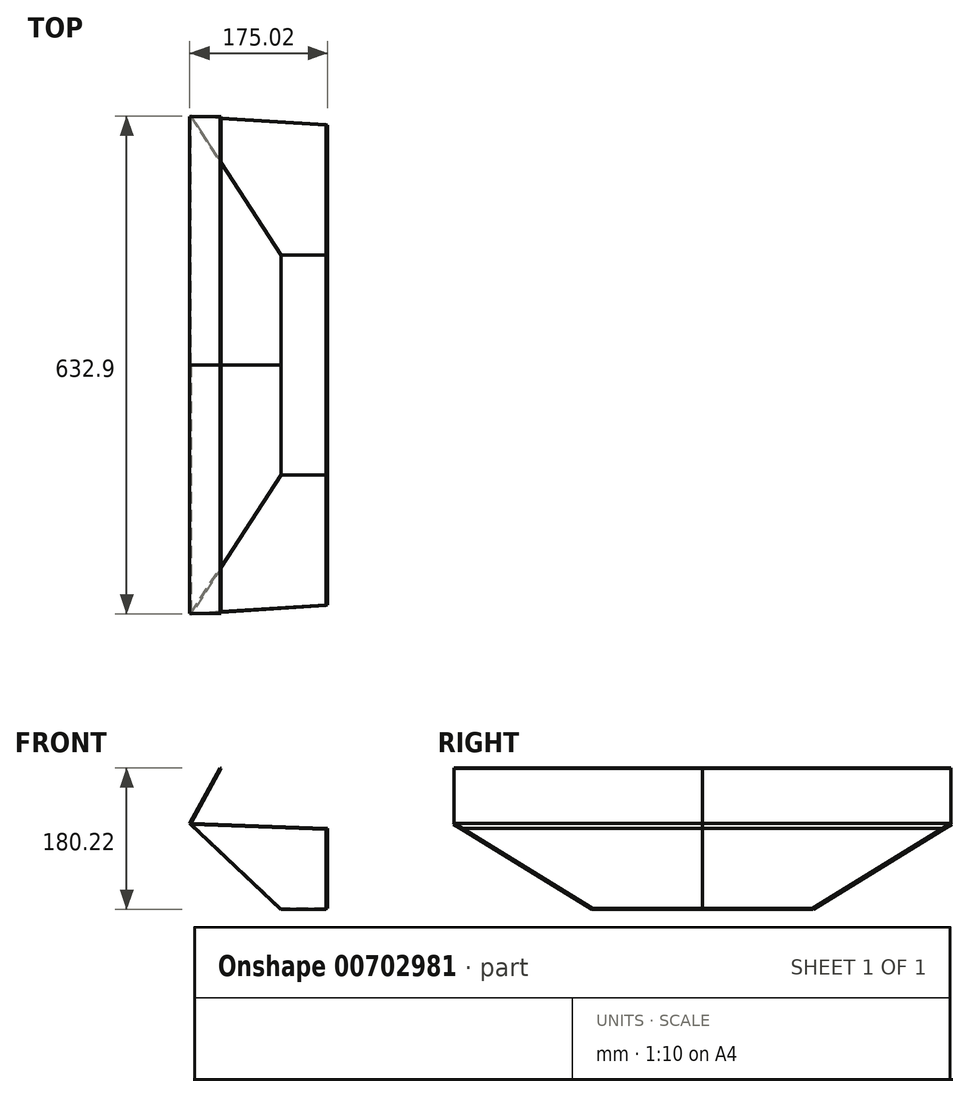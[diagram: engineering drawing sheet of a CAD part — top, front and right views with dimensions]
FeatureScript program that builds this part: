
annotation { "Feature Type Name" : "Feature", "Feature Type Description" : "" }
export const myFeature = defineFeature(function(context is Context, id is Id, definition is map)
    precondition{}
    {
        {
            var Q0;
            Q0=qCreatedBy(makeId("Right.planeOp"),FACE);
            var sketch = newSketch(context, id + "F0", { "sketchPlane" : qUnion([Q0])});
            skPoint(sketch, "E0.middle", {"position": v(0, 0) * mm});
            skLineSegment(sketch, "E1", {"start": v(304.8, 151.03) * mm, "end": v(139.7, 49.43) * mm});
            skLineSegment(sketch, "E2", {"start": v(0, 49.43) * mm, "end": v(0, 151.03) * mm});
            skLineSegment(sketch, "E3", {"start": v(304.8, 151.03) * mm, "end": v(0, 151.03) * mm});
            skLineSegment(sketch, "E4", {"start": v(139.7, 49.43) * mm, "end": v(0, 49.43) * mm});
            skSolve(sketch);
        }
        {
            var Q0;
            Q0 = qSketchRegion(id + "F0", true);
            extrude(context, id + "F1", {"entities" : qUnion([Q0]), "depth" : 1.59 * mm, "offsetDistance" : 25.4 * mm});
        }
        {
            var Q0;
            Q0=makeQuery(id+"F1.opExtrude","SWEPT_FACE",FACE,{"disambiguationData":[OSD([sQuery(id+"F0.wireOp",EDGE,"E1")])]});
            var sketch = newSketch(context, id + "F2", { "sketchPlane" : qUnion([Q0])});
            skLineSegment(sketch, "E5", {"start": v(0, -144.88) * mm, "end": v(-57.15, -144.88) * mm});
            skLineSegment(sketch, "E6", {"start": v(-57.15, -144.88) * mm, "end": v(-171.45, -351.44) * mm});
            skLineSegment(sketch, "E7", {"start": v(0, -338.74) * mm, "end": v(-171.45, -351.44) * mm});
            skSolve(sketch);
        }
        {
            var Q0;
            Q0=makeQuery(id+"F2.imprint","IMPRINT",FACE,{"disambiguationData":[TD([[makeQuery(id+"F2.imprint","IMPRINT",EDGE,{"derivedFrom":sQuery(id+"F2.wireOp",EDGE,"E5")}),1.0]])]});
            extrude(context, id + "F3", {"entities" : qUnion([Q0]), "depth" : 1.59 * mm, "offsetDistance" : 25.4 * mm});
        }
        {
            var Q0;
            Q0=makeQuery(id+"F1.opExtrude","SWEPT_FACE",FACE,{"disambiguationData":[OSD([sQuery(id+"F0.wireOp",EDGE,"E4")])]});
            var sketch = newSketch(context, id + "F4", { "sketchPlane" : qUnion([Q0])});
            skLineSegment(sketch, "E8", {"start": v(0, -139.7) * mm, "end": v(-57.15, -139.7) * mm});
            skLineSegment(sketch, "E9", {"start": v(-57.15, -139.7) * mm, "end": v(-57.15, 0) * mm});
            skLineSegment(sketch, "E10", {"start": v(-57.15, 0) * mm, "end": v(0, 0) * mm});
            skSolve(sketch);
        }
        {
            var Q0;
            Q0=sQuery(id+"F4.wireOp",VERTEX,"E10.start");
            var Q1;
            Q1=sQuery(id+"F4.wireOp",VERTEX,"E9.start");
            var Q2;
            Q2=makeQuery(id+"F3.opExtrude","CAP_VERTEX",VERTEX,{"disambiguationData":[OSD([sQuery(id+"F2.wireOp",EDGE,"E6"),sQuery(id+"F2.wireOp",EDGE,"E7")])],"isStart":true});
            cPlane(context, id + "F5", {"entities" : qUnion([Q0, Q1, Q2]), "cplaneType" : CPlaneType.THREE_POINT, "offset" : 25.4 * mm, "width" : 152.4 * mm, "height" : 152.4 * mm});
        }
        {
            var Q0;
            Q0=qCreatedBy(id+"F5.planeOp",FACE);
            var sketch = newSketch(context, id + "F6", { "sketchPlane" : qUnion([Q0])});
            skLineSegment(sketch, "E11", {"start": v(-75.48, 0) * mm, "end": v(-75.48, -139.7) * mm});
            skLineSegment(sketch, "E12", {"start": v(-232.91, 0) * mm, "end": v(-75.48, 0) * mm});
            skLineSegment(sketch, "E13", {"start": v(-232.91, 0) * mm, "end": v(-232.91, -315.62) * mm});
            skLineSegment(sketch, "E14", {"start": v(-232.91, -315.62) * mm, "end": v(-75.48, -139.7) * mm});
            skSolve(sketch);
        }
        {
            var Q0;
            Q0=makeQuery(id+"F6.imprint","IMPRINT",FACE,{"disambiguationData":[TD([[makeQuery(id+"F6.imprint","IMPRINT",EDGE,{"derivedFrom":sQuery(id+"F6.wireOp",EDGE,"E11")}),-1.0]])]});
            extrude(context, id + "F7", {"entities" : qUnion([Q0]), "depth" : 1.59 * mm, "offsetDistance" : 25.4 * mm});
        }
        {
            var Q0;
            Q0=makeQuery(id+"F7.opExtrude","SWEPT_FACE",FACE,{"disambiguationData":[OSD([sQuery(id+"F6.wireOp",EDGE,"E12")])]});
            var sketch = newSketch(context, id + "F8", { "sketchPlane" : qUnion([Q0])});
            skLineSegment(sketch, "E15", {"start": v(-172.54, 156.53) * mm, "end": v(-173.43, 157.37) * mm});
            skLineSegment(sketch, "E16", {"start": v(-173.43, 157.37) * mm, "end": v(-134.74, 228.3) * mm});
            skLineSegment(sketch, "E17", {"start": v(-134.74, 228.3) * mm, "end": v(-133.35, 227.54) * mm});
            skLineSegment(sketch, "E18", {"start": v(-133.35, 227.54) * mm, "end": v(-171.45, 157.69) * mm});
            skSolve(sketch);
        }
        {
            var Q0;
            Q0=makeQuery(id+"F8.imprint","IMPRINT",FACE,{"disambiguationData":[TD([[makeQuery(id+"F8.imprint","IMPRINT",EDGE,{"derivedFrom":sQuery(id+"F8.wireOp",EDGE,"E15")}),-1.0]])]});
            extrude(context, id + "F9", {"entities" : qUnion([Q0]), "operationType" : NewBodyOperationType.ADD, "oppositeDirection" : true, "depth" : 315.62 * mm, "offsetDistance" : 25.4 * mm});
        }
        {
            var Q0;
            Q0=makeQuery(id+"F7.opExtrude","SWEPT_BODY",BODY,{"disambiguationData":[OSD([sQuery(id+"F6.wireOp",EDGE,"E11"),sQuery(id+"F6.wireOp",EDGE,"E12"),sQuery(id+"F6.wireOp",EDGE,"E13"),sQuery(id+"F6.wireOp",EDGE,"E14")])]});
            var Q1;
            Q1=makeQuery(id+"F3.opExtrude","SWEPT_BODY",BODY,{"disambiguationData":[OSD([sQuery(id+"F0.wireOp",EDGE,"E1"),sQuery(id+"F2.wireOp",EDGE,"E5"),sQuery(id+"F2.wireOp",EDGE,"E6"),sQuery(id+"F2.wireOp",EDGE,"E7")])]});
            var Q2;
            Q2=makeQuery(id+"F1.opExtrude","SWEPT_BODY",BODY,{"disambiguationData":[OSD([sQuery(id+"F0.wireOp",EDGE,"E1"),sQuery(id+"F0.wireOp",EDGE,"E2"),sQuery(id+"F0.wireOp",EDGE,"E3"),sQuery(id+"F0.wireOp",EDGE,"E4")])]});
            var Q3;
            Q3=qCreatedBy(makeId("Front.planeOp"),FACE);
            mirror(context, id + "F10", {"entities" : qUnion([Q0, Q1, Q2]), "mirrorPlane" : qUnion([Q3])});
        }
    });
